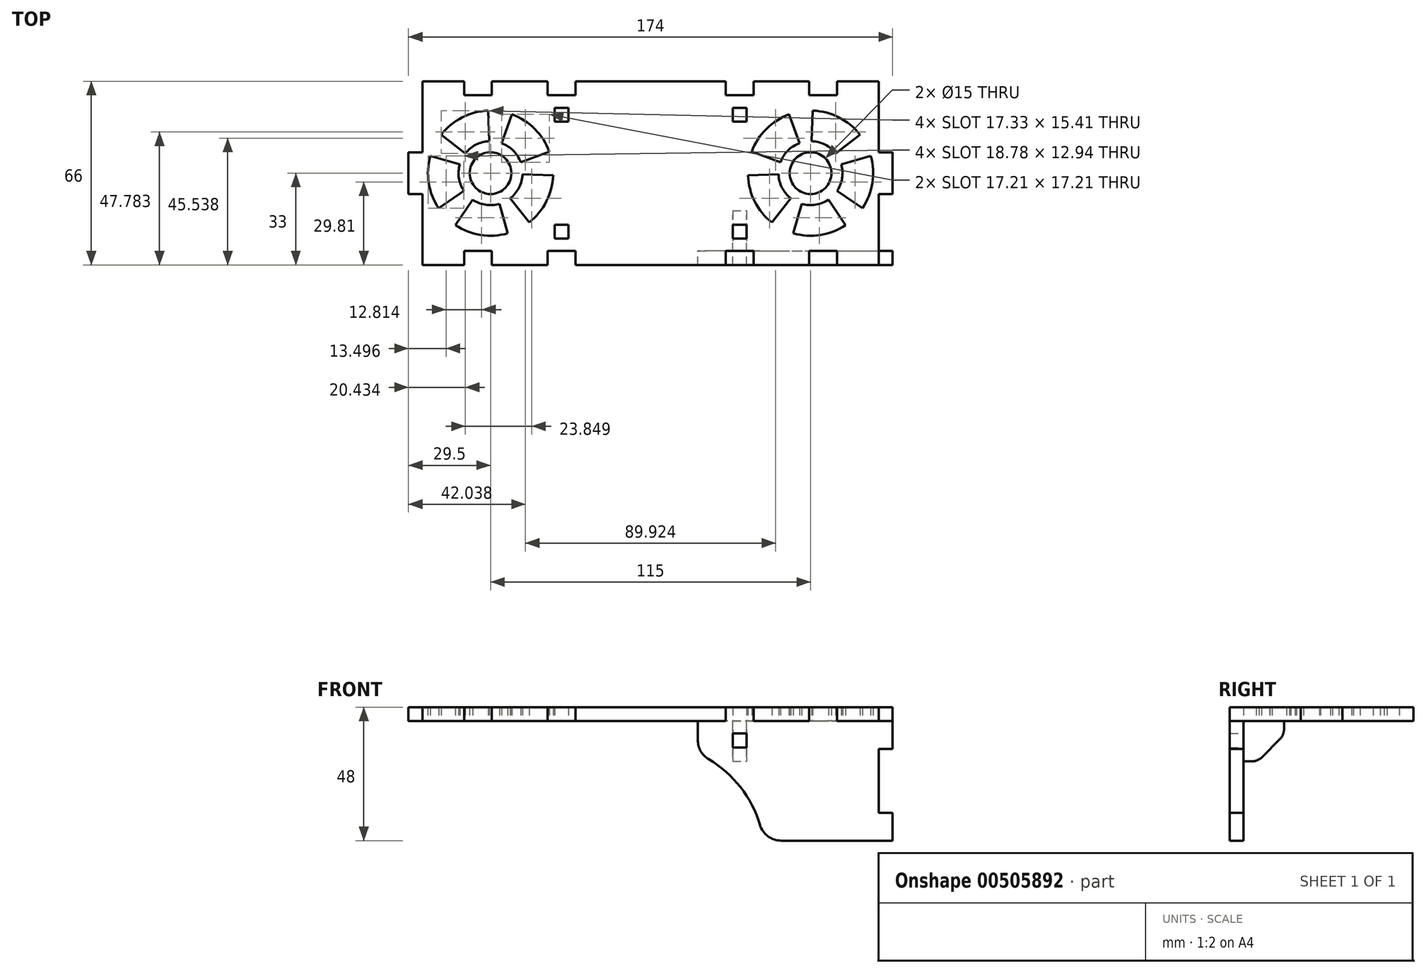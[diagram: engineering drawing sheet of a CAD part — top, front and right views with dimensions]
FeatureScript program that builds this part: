
annotation { "Feature Type Name" : "Feature", "Feature Type Description" : "" }
export const myFeature = defineFeature(function(context is Context, id is Id, definition is map)
    precondition{}
    {
        {
            var Q0;
            Q0=qCreatedBy(makeId("Top.planeOp"),FACE);
            var sketch = newSketch(context, id + "F0", { "sketchPlane" : qUnion([Q0])});
            skLineSegment(sketch, "E0.bottom", {"start": v(-82, 33) * mm, "end": v(82, 33) * mm});
            skLineSegment(sketch, "E0.top", {"start": v(-82, -33) * mm, "end": v(82, -33) * mm});
            skLineSegment(sketch, "E0.left", {"start": v(-82, 33) * mm, "end": v(-82, -33) * mm});
            skLineSegment(sketch, "E0.right", {"start": v(82, 33) * mm, "end": v(82, -33) * mm});
            skPoint(sketch, "E0.middle", {"position": v(0, 0) * mm});
            skLineSegment(sketch, "E1.bottom", {"start": v(-82, 7.5) * mm, "end": v(-87, 7.5) * mm});
            skLineSegment(sketch, "E1.top", {"start": v(-82, -7.5) * mm, "end": v(-87, -7.5) * mm});
            skLineSegment(sketch, "E1.left", {"start": v(-82, 7.5) * mm, "end": v(-82, -7.5) * mm});
            skLineSegment(sketch, "E1.right", {"start": v(-87, 7.5) * mm, "end": v(-87, -7.5) * mm});
            skPoint(sketch, "E1.middle", {"position": v(-84.5, 0) * mm});
            skLineSegment(sketch, "E2.bottom", {"start": v(82, 7.5) * mm, "end": v(87, 7.5) * mm});
            skLineSegment(sketch, "E2.top", {"start": v(82, -7.5) * mm, "end": v(87, -7.5) * mm});
            skLineSegment(sketch, "E2.left", {"start": v(82, 7.5) * mm, "end": v(82, -7.5) * mm});
            skLineSegment(sketch, "E2.right", {"start": v(87, 7.5) * mm, "end": v(87, -7.5) * mm});
            skPoint(sketch, "E2.middle", {"position": v(84.5, 0) * mm});
            skLineSegment(sketch, "E3", {"start": v(0, 0) * mm, "end": v(0, 23.82) * mm, "construction": true});
            skCircle(sketch, "E4", {"center": v(-57.5, 0) * mm, "radius": 7.5 * mm});
            skLineSegment(sketch, "E5", {"start": v(-57.5, 0) * mm, "end": v(-57.5, 16.42) * mm, "construction": true});
            skArc(sketch, "E6", {"start": v(-46.7, 3.93) * mm, "mid": v(-49.37, 8.13) * mm, "end": v(-53.57, 10.8) * mm});
            skArc(sketch, "E7", {"start": v(-36.36, 7.7) * mm, "mid": v(-41.6, 15.9) * mm, "end": v(-49.8, 21.14) * mm});
            skLineSegment(sketch, "E8", {"start": v(-49.8, 21.14) * mm, "end": v(-53.57, 10.8) * mm});
            skLineSegment(sketch, "E9", {"start": v(-36.36, 7.7) * mm, "end": v(-46.7, 3.93) * mm});
            skLineSegment(sketch, "E10", {"start": v(-57.5, 0) * mm, "end": v(-40.16, 0) * mm, "construction": true});
            skArc(sketch, "E11.1.0", {"start": v(-58.29, 22.49) * mm, "mid": v(-67.71, 20.05) * mm, "end": v(-75.23, 13.85) * mm});
            skLineSegment(sketch, "E11.1.1", {"start": v(-58.29, 22.49) * mm, "end": v(-57.9, 11.5) * mm});
            skArc(sketch, "E11.1.2", {"start": v(-57.9, 11.5) * mm, "mid": v(-62.72, 10.25) * mm, "end": v(-66.56, 7.08) * mm});
            skLineSegment(sketch, "E11.1.3", {"start": v(-75.23, 13.85) * mm, "end": v(-66.56, 7.08) * mm});
            skArc(sketch, "E11.2.0", {"start": v(-79.13, 6.2) * mm, "mid": v(-79.72, -3.52) * mm, "end": v(-76.15, -12.58) * mm});
            skLineSegment(sketch, "E11.2.1", {"start": v(-79.13, 6.2) * mm, "end": v(-68.55, 3.17) * mm});
            skArc(sketch, "E11.2.2", {"start": v(-68.55, 3.17) * mm, "mid": v(-68.86, -1.8) * mm, "end": v(-67.03, -6.43) * mm});
            skLineSegment(sketch, "E11.2.3", {"start": v(-76.15, -12.58) * mm, "end": v(-67.03, -6.43) * mm});
            skArc(sketch, "E11.3.0", {"start": v(-70.08, -18.65) * mm, "mid": v(-61.02, -22.22) * mm, "end": v(-51.3, -21.63) * mm});
            skLineSegment(sketch, "E11.3.1", {"start": v(-70.08, -18.65) * mm, "end": v(-63.93, -9.53) * mm});
            skArc(sketch, "E11.3.2", {"start": v(-63.93, -9.53) * mm, "mid": v(-59.3, -11.36) * mm, "end": v(-54.33, -11.05) * mm});
            skLineSegment(sketch, "E11.3.3", {"start": v(-51.3, -21.63) * mm, "end": v(-54.33, -11.05) * mm});
            skArc(sketch, "E11.4.0", {"start": v(-43.65, -17.73) * mm, "mid": v(-37.45, -10.21) * mm, "end": v(-35.01, -0.79) * mm});
            skLineSegment(sketch, "E11.4.1", {"start": v(-43.65, -17.73) * mm, "end": v(-50.42, -9.06) * mm});
            skArc(sketch, "E11.4.2", {"start": v(-50.42, -9.06) * mm, "mid": v(-47.25, -5.22) * mm, "end": v(-46, -0.4) * mm});
            skLineSegment(sketch, "E11.4.3", {"start": v(-35.01, -0.79) * mm, "end": v(-46, -0.4) * mm});
            skCircle(sketch, "E12.MirrorC", {"center": v(57.5, 0) * mm, "radius": 7.5 * mm});
            skArc(sketch, "E13.MirrorCS", {"start": v(46.7, 3.93) * mm, "mid": v(49.37, 8.13) * mm, "end": v(53.57, 10.8) * mm});
            skLineSegment(sketch, "E14.MirrorCS", {"start": v(49.8, 21.14) * mm, "end": v(53.57, 10.8) * mm});
            skArc(sketch, "E15.MirrorCS", {"start": v(36.36, 7.7) * mm, "mid": v(41.6, 15.9) * mm, "end": v(49.8, 21.14) * mm});
            skLineSegment(sketch, "E16.MirrorCS", {"start": v(36.36, 7.7) * mm, "end": v(46.7, 3.93) * mm});
            skLineSegment(sketch, "E17.MirrorCS", {"start": v(35.01, -0.79) * mm, "end": v(46, -0.4) * mm});
            skArc(sketch, "E18.MirrorCS", {"start": v(43.65, -17.73) * mm, "mid": v(37.45, -10.21) * mm, "end": v(35.01, -0.79) * mm});
            skLineSegment(sketch, "E19.MirrorCS", {"start": v(43.65, -17.73) * mm, "end": v(50.42, -9.06) * mm});
            skArc(sketch, "E20.MirrorCS", {"start": v(50.42, -9.06) * mm, "mid": v(47.25, -5.22) * mm, "end": v(46, -0.4) * mm});
            skArc(sketch, "E21.MirrorCS", {"start": v(63.93, -9.53) * mm, "mid": v(59.3, -11.36) * mm, "end": v(54.33, -11.05) * mm});
            skLineSegment(sketch, "E22.MirrorCS", {"start": v(51.3, -21.63) * mm, "end": v(54.33, -11.05) * mm});
            skArc(sketch, "E23.MirrorCS", {"start": v(70.08, -18.65) * mm, "mid": v(61.02, -22.22) * mm, "end": v(51.3, -21.63) * mm});
            skLineSegment(sketch, "E24.MirrorCS", {"start": v(70.08, -18.65) * mm, "end": v(63.93, -9.53) * mm});
            skLineSegment(sketch, "E25.MirrorCS", {"start": v(76.15, -12.58) * mm, "end": v(67.03, -6.43) * mm});
            skArc(sketch, "E26.MirrorCS", {"start": v(68.55, 3.17) * mm, "mid": v(68.86, -1.8) * mm, "end": v(67.03, -6.43) * mm});
            skLineSegment(sketch, "E27.MirrorCS", {"start": v(79.13, 6.2) * mm, "end": v(68.55, 3.17) * mm});
            skArc(sketch, "E28.MirrorCS", {"start": v(79.13, 6.2) * mm, "mid": v(79.72, -3.52) * mm, "end": v(76.15, -12.58) * mm});
            skLineSegment(sketch, "E29.MirrorCS", {"start": v(75.23, 13.85) * mm, "end": v(66.56, 7.08) * mm});
            skArc(sketch, "E30.MirrorCS", {"start": v(58.29, 22.49) * mm, "mid": v(67.71, 20.05) * mm, "end": v(75.23, 13.85) * mm});
            skLineSegment(sketch, "E31.MirrorCS", {"start": v(58.29, 22.49) * mm, "end": v(57.9, 11.5) * mm});
            skArc(sketch, "E32.MirrorCS", {"start": v(57.9, 11.5) * mm, "mid": v(62.72, 10.25) * mm, "end": v(66.56, 7.08) * mm});
            skLineSegment(sketch, "E33.bottom", {"start": v(67, 33) * mm, "end": v(57, 33) * mm});
            skLineSegment(sketch, "E33.top", {"start": v(67, 28) * mm, "end": v(57, 28) * mm});
            skLineSegment(sketch, "E33.left", {"start": v(67, 33) * mm, "end": v(67, 28) * mm});
            skLineSegment(sketch, "E33.right", {"start": v(57, 33) * mm, "end": v(57, 28) * mm});
            skLineSegment(sketch, "E34.bottom", {"start": v(37, 33) * mm, "end": v(27, 33) * mm});
            skLineSegment(sketch, "E34.top", {"start": v(37, 28) * mm, "end": v(27, 28) * mm});
            skLineSegment(sketch, "E34.left", {"start": v(37, 33) * mm, "end": v(37, 28) * mm});
            skLineSegment(sketch, "E34.right", {"start": v(27, 33) * mm, "end": v(27, 28) * mm});
            skLineSegment(sketch, "E35.bottom", {"start": v(34.5, 23.5) * mm, "end": v(29.5, 23.5) * mm});
            skLineSegment(sketch, "E35.top", {"start": v(34.5, 18.5) * mm, "end": v(29.5, 18.5) * mm});
            skLineSegment(sketch, "E35.left", {"start": v(34.5, 23.5) * mm, "end": v(34.5, 18.5) * mm});
            skLineSegment(sketch, "E35.right", {"start": v(29.5, 23.5) * mm, "end": v(29.5, 18.5) * mm});
            skPoint(sketch, "E35.middle", {"position": v(32, 21) * mm});
            skLineSegment(sketch, "E36", {"start": v(0, 0) * mm, "end": v(17.94, 0) * mm, "construction": true});
            skPoint(sketch, "E37", {"position": v(32, 28) * mm});
            skLineSegment(sketch, "E38.MirrorCS", {"start": v(-34.5, 23.5) * mm, "end": v(-29.5, 23.5) * mm});
            skLineSegment(sketch, "E39.MirrorCS", {"start": v(-29.5, 23.5) * mm, "end": v(-29.5, 18.5) * mm});
            skLineSegment(sketch, "E40.MirrorCS", {"start": v(-34.5, 18.5) * mm, "end": v(-29.5, 18.5) * mm});
            skLineSegment(sketch, "E41.MirrorCS", {"start": v(-34.5, 23.5) * mm, "end": v(-34.5, 18.5) * mm});
            skLineSegment(sketch, "E42.MirrorCS", {"start": v(-37, 33) * mm, "end": v(-37, 28) * mm});
            skLineSegment(sketch, "E43.MirrorCS", {"start": v(-37, 28) * mm, "end": v(-27, 28) * mm});
            skLineSegment(sketch, "E44.MirrorCS", {"start": v(-27, 33) * mm, "end": v(-27, 28) * mm});
            skLineSegment(sketch, "E45.MirrorCS", {"start": v(-57, 33) * mm, "end": v(-57, 28) * mm});
            skLineSegment(sketch, "E46.MirrorCS", {"start": v(-67, 28) * mm, "end": v(-57, 28) * mm});
            skLineSegment(sketch, "E47.MirrorCS", {"start": v(-67, 33) * mm, "end": v(-67, 28) * mm});
            skLineSegment(sketch, "E48.MirrorCS", {"start": v(-57, -33) * mm, "end": v(-57, -28) * mm});
            skLineSegment(sketch, "E49.MirrorCS", {"start": v(-67, -28) * mm, "end": v(-57, -28) * mm});
            skLineSegment(sketch, "E50.MirrorCS", {"start": v(-67, -33) * mm, "end": v(-67, -28) * mm});
            skLineSegment(sketch, "E51.MirrorCS", {"start": v(-37, -33) * mm, "end": v(-37, -28) * mm});
            skLineSegment(sketch, "E52.MirrorCS", {"start": v(-37, -28) * mm, "end": v(-27, -28) * mm});
            skLineSegment(sketch, "E53.MirrorCS", {"start": v(-27, -33) * mm, "end": v(-27, -28) * mm});
            skLineSegment(sketch, "E54.MirrorCS", {"start": v(-34.5, -23.5) * mm, "end": v(-29.5, -23.5) * mm});
            skLineSegment(sketch, "E55.MirrorCS", {"start": v(-29.5, -23.5) * mm, "end": v(-29.5, -18.5) * mm});
            skLineSegment(sketch, "E56.MirrorCS", {"start": v(-34.5, -18.5) * mm, "end": v(-29.5, -18.5) * mm});
            skLineSegment(sketch, "E57.MirrorCS", {"start": v(-34.5, -23.5) * mm, "end": v(-34.5, -18.5) * mm});
            skLineSegment(sketch, "E58.MirrorCS", {"start": v(37, -33) * mm, "end": v(37, -28) * mm});
            skLineSegment(sketch, "E59.MirrorCS", {"start": v(37, -28) * mm, "end": v(27, -28) * mm});
            skLineSegment(sketch, "E60.MirrorCS", {"start": v(27, -33) * mm, "end": v(27, -28) * mm});
            skLineSegment(sketch, "E61.MirrorCS", {"start": v(57, -33) * mm, "end": v(57, -28) * mm});
            skLineSegment(sketch, "E62.MirrorCS", {"start": v(67, -28) * mm, "end": v(57, -28) * mm});
            skLineSegment(sketch, "E63.MirrorCS", {"start": v(67, -33) * mm, "end": v(67, -28) * mm});
            skLineSegment(sketch, "E64.MirrorCS", {"start": v(34.5, -23.5) * mm, "end": v(29.5, -23.5) * mm});
            skLineSegment(sketch, "E65.MirrorCS", {"start": v(34.5, -23.5) * mm, "end": v(34.5, -18.5) * mm});
            skLineSegment(sketch, "E66.MirrorCS", {"start": v(34.5, -18.5) * mm, "end": v(29.5, -18.5) * mm});
            skLineSegment(sketch, "E67.MirrorCS", {"start": v(29.5, -23.5) * mm, "end": v(29.5, -18.5) * mm});
            skSolve(sketch);
        }
        {
            var Q0;
            {var subQ4=sQuery(id+"F0.wireOp",EDGE,"E0.bottom");Q0=makeQuery(id+"F0.imprint","IMPRINT",FACE,{"disambiguationData":[TD([[makeQuery(id+"F0.imprint","IMPRINT",EDGE,{"derivedFrom":subQ4}),-1.0]])]});}
            var Q1;
            Q1=makeQuery(id+"F0.imprint","IMPRINT",FACE,{"disambiguationData":[TD([[makeQuery(id+"F0.imprint","IMPRINT",EDGE,{"derivedFrom":sQuery(id+"F0.wireOp",EDGE,"E1.bottom")}),1.0]])]});
            var Q2;
            Q2=makeQuery(id+"F0.imprint","IMPRINT",FACE,{"disambiguationData":[TD([[makeQuery(id+"F0.imprint","IMPRINT",EDGE,{"derivedFrom":sQuery(id+"F0.wireOp",EDGE,"E2.bottom")}),-1.0]])]});
            extrude(context, id + "F1", {"entities" : qUnion([Q0, Q1, Q2]), "depth" : 5 * mm, "offsetDistance" : 25 * mm});
        }
        {
            var Q0;
            Q0=makeQuery(id+"F1.opExtrude","SWEPT_FACE",FACE,{"disambiguationData":[OSD([sQuery(id+"F0.wireOp",EDGE,"E59.MirrorCS")])]});
            var sketch = newSketch(context, id + "F2", { "sketchPlane" : qUnion([Q0])});
            skLineSegment(sketch, "E68.0", {"start": v(27, 5) * mm, "end": v(27, 0) * mm});
            skLineSegment(sketch, "E68.1", {"start": v(37, 5) * mm, "end": v(27, 5) * mm});
            skLineSegment(sketch, "E68.2", {"start": v(37, 5) * mm, "end": v(37, 0) * mm});
            skLineSegment(sketch, "E68.3", {"start": v(57, 5) * mm, "end": v(57, 0) * mm});
            skLineSegment(sketch, "E68.4", {"start": v(67, 5) * mm, "end": v(57, 5) * mm});
            skLineSegment(sketch, "E68.5", {"start": v(67, 5) * mm, "end": v(67, 0) * mm});
            skLineSegment(sketch, "E69", {"start": v(37, 0) * mm, "end": v(57, 0) * mm});
            skLineSegment(sketch, "E70", {"start": v(67, 0) * mm, "end": v(82, 0) * mm});
            skCircle(sketch, "E71", {"center": v(0, -49) * mm, "radius": 40 * mm, "construction": true});
            skArc(sketch, "E72", {"start": v(39.3, -37.29) * mm, "mid": v(32.33, -23.78) * mm, "end": v(20.92, -13.74) * mm});
            skLineSegment(sketch, "E73", {"start": v(27, 0) * mm, "end": v(17, 0) * mm});
            skLineSegment(sketch, "E74", {"start": v(17, 0) * mm, "end": v(17, -6.86) * mm});
            skLineSegment(sketch, "E75", {"start": v(46.96, -43) * mm, "end": v(82, -43) * mm});
            skLineSegment(sketch, "E76", {"start": v(82, 0) * mm, "end": v(82, -43) * mm});
            skPoint(sketch, "E77.visualSharp", {"position": v(17, -11.7) * mm});
            skArc(sketch, "E77.filletArc", {"start": v(17, -6.86) * mm, "mid": v(18.05, -10.82) * mm, "end": v(20.92, -13.74) * mm});
            skPoint(sketch, "E78.visualSharp", {"position": v(40.56, -43) * mm});
            skArc(sketch, "E78.filletArc", {"start": v(39.3, -37.29) * mm, "mid": v(42.18, -41.41) * mm, "end": v(46.96, -43) * mm});
            skLineSegment(sketch, "E79.bottom", {"start": v(34.5, -4.5) * mm, "end": v(29.5, -4.5) * mm});
            skLineSegment(sketch, "E79.top", {"start": v(34.5, -9.5) * mm, "end": v(29.5, -9.5) * mm});
            skLineSegment(sketch, "E79.left", {"start": v(34.5, -4.5) * mm, "end": v(34.5, -9.5) * mm});
            skLineSegment(sketch, "E79.right", {"start": v(29.5, -4.5) * mm, "end": v(29.5, -9.5) * mm});
            skPoint(sketch, "E79.middle", {"position": v(32, -7) * mm});
            skPoint(sketch, "E80", {"position": v(32, 5) * mm});
            skLineSegment(sketch, "E81.bottom", {"start": v(82, 0) * mm, "end": v(87, 0) * mm});
            skLineSegment(sketch, "E81.top", {"start": v(82, -10) * mm, "end": v(87, -10) * mm});
            skLineSegment(sketch, "E81.left", {"start": v(82, 0) * mm, "end": v(82, -10) * mm});
            skLineSegment(sketch, "E81.right", {"start": v(87, 0) * mm, "end": v(87, -10) * mm});
            skLineSegment(sketch, "E82.bottom", {"start": v(82, -43) * mm, "end": v(87, -43) * mm});
            skLineSegment(sketch, "E82.top", {"start": v(82, -33) * mm, "end": v(87, -33) * mm});
            skLineSegment(sketch, "E82.left", {"start": v(82, -43) * mm, "end": v(82, -33) * mm});
            skLineSegment(sketch, "E82.right", {"start": v(87, -43) * mm, "end": v(87, -33) * mm});
            skSolve(sketch);
        }
        {
            var Q0;
            Q0 = qSketchRegion(id + "F2", true);
            extrude(context, id + "F3", {"entities" : qUnion([Q0]), "depth" : 5 * mm, "offsetDistance" : 25 * mm});
        }
        {
            var Q0;
            Q0=makeQuery(id+"F1.opExtrude","SWEPT_FACE",FACE,{"disambiguationData":[OSD([sQuery(id+"F0.wireOp",EDGE,"E65.MirrorCS")])]});
            var sketch = newSketch(context, id + "F4", { "sketchPlane" : qUnion([Q0])});
            skLineSegment(sketch, "E83.0", {"start": v(18.5, 5) * mm, "end": v(18.5, 0) * mm});
            skLineSegment(sketch, "E83.1", {"start": v(23.5, 5) * mm, "end": v(18.5, 5) * mm});
            skLineSegment(sketch, "E83.2", {"start": v(23.5, 5) * mm, "end": v(23.5, 0) * mm});
            skLineSegment(sketch, "E83.3", {"start": v(33, -4.5) * mm, "end": v(28, -4.5) * mm});
            skLineSegment(sketch, "E83.4", {"start": v(33, -4.5) * mm, "end": v(33, -9.5) * mm});
            skLineSegment(sketch, "E83.5", {"start": v(33, -9.5) * mm, "end": v(28, -9.5) * mm});
            skLineSegment(sketch, "E84", {"start": v(28, -4.5) * mm, "end": v(28, 0) * mm});
            skLineSegment(sketch, "E85", {"start": v(28, 0) * mm, "end": v(23.5, 0) * mm});
            skLineSegment(sketch, "E86", {"start": v(28, -9.5) * mm, "end": v(28, -14.5) * mm});
            skLineSegment(sketch, "E87", {"start": v(28, -14.5) * mm, "end": v(25, -14.5) * mm});
            skLineSegment(sketch, "E88", {"start": v(21.38, -13) * mm, "end": v(14.95, -6.52) * mm});
            skLineSegment(sketch, "E89", {"start": v(13.5, -3) * mm, "end": v(13.5, 0) * mm});
            skLineSegment(sketch, "E90", {"start": v(13.5, 0) * mm, "end": v(18.5, 0) * mm});
            skPoint(sketch, "E91.visualSharp", {"position": v(13.5, -5.06) * mm});
            skArc(sketch, "E91.filletArc", {"start": v(13.5, -3) * mm, "mid": v(13.88, -4.9) * mm, "end": v(14.95, -6.52) * mm});
            skPoint(sketch, "E92.visualSharp", {"position": v(22.88, -14.5) * mm});
            skArc(sketch, "E92.filletArc", {"start": v(21.38, -13) * mm, "mid": v(23.04, -14.1) * mm, "end": v(25, -14.5) * mm});
            skSolve(sketch);
        }
        {
            var Q0;
            Q0 = qSketchRegion(id + "F4", true);
            extrude(context, id + "F5", {"entities" : qUnion([Q0]), "depth" : 5 * mm, "offsetDistance" : 25 * mm});
        }
    });
